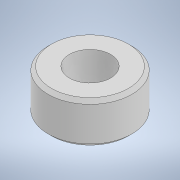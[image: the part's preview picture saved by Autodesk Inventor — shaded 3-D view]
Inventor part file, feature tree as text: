
AUTODESK INVENTOR PART (.ipt)
format: ipt  version: 2020 (Build 240168000, 168)  size: 105,984 bytes
history: native  units: mm
features: extrude x1, chamfer x1, sketch x1
ambient origin geometry x8: Origin, YZ Plane, XZ Plane, XY Plane, X Axis, Y Axis, Z Axis, Center Point
bodies: Solid1 (feature_tree)
feature tree (3):
  extrude  "Extrusion1"  Depth=3.0mm
  chamfer  "Chamfer1"  Distance=3.0mm
  sketch  "Sketch1"  dims[d0=3.0mm d1=6.1mm d2=3.0mm d3=0.0mm d4=0.25mm d5=2.0mm d6=45.0deg]
